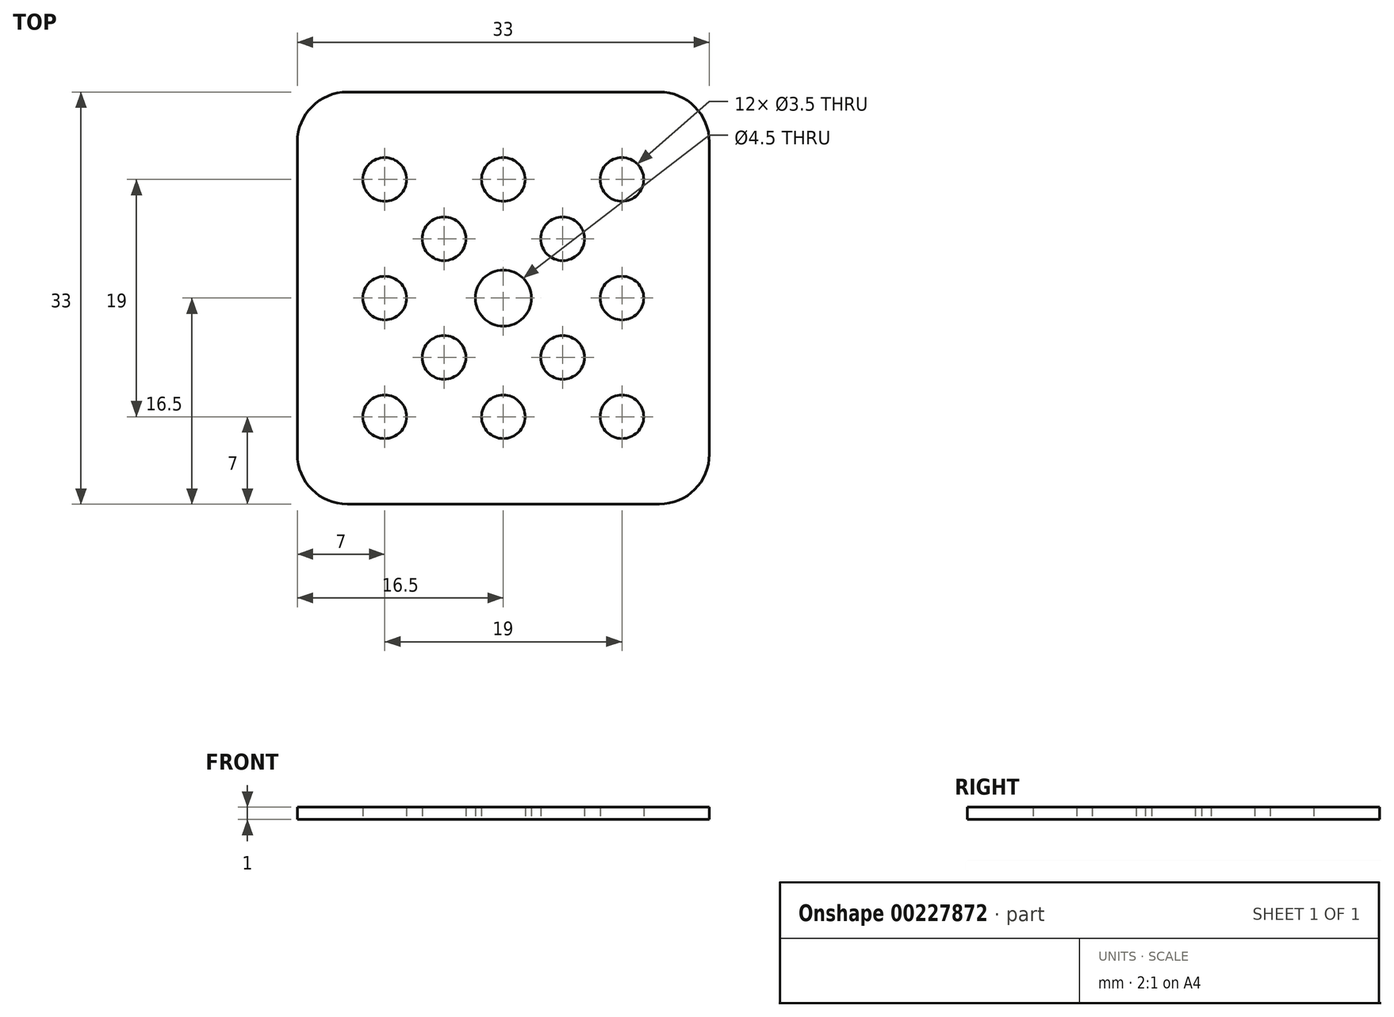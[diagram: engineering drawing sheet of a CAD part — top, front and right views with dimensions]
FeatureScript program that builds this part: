
annotation { "Feature Type Name" : "Feature", "Feature Type Description" : "" }
export const myFeature = defineFeature(function(context is Context, id is Id, definition is map)
    precondition{}
    {
        {
            var Q0;
            Q0=qCreatedBy(makeId("Top.planeOp"),FACE);
            var sketch = newSketch(context, id + "F0", { "sketchPlane" : qUnion([Q0])});
            skLineSegment(sketch, "E0.bottom", {"start": v(12.5, 16.5) * mm, "end": v(-12.5, 16.5) * mm});
            skLineSegment(sketch, "E0.top", {"start": v(12.5, -16.5) * mm, "end": v(-12.5, -16.5) * mm});
            skLineSegment(sketch, "E0.left", {"start": v(16.5, 12.5) * mm, "end": v(16.5, -12.5) * mm});
            skLineSegment(sketch, "E0.right", {"start": v(-16.5, 12.5) * mm, "end": v(-16.5, -12.5) * mm});
            skPoint(sketch, "E1.visualSharp", {"position": v(-16.5, 16.5) * mm});
            skArc(sketch, "E1.filletArc", {"start": v(-12.5, 16.5) * mm, "mid": v(-15.33, 15.33) * mm, "end": v(-16.5, 12.5) * mm});
            skPoint(sketch, "E2.visualSharp", {"position": v(16.5, 16.5) * mm});
            skArc(sketch, "E2.filletArc", {"start": v(16.5, 12.5) * mm, "mid": v(15.33, 15.33) * mm, "end": v(12.5, 16.5) * mm});
            skPoint(sketch, "E3.visualSharp", {"position": v(16.5, -16.5) * mm});
            skArc(sketch, "E3.filletArc", {"start": v(12.5, -16.5) * mm, "mid": v(15.33, -15.33) * mm, "end": v(16.5, -12.5) * mm});
            skPoint(sketch, "E4.visualSharp", {"position": v(-16.5, -16.5) * mm});
            skArc(sketch, "E4.filletArc", {"start": v(-16.5, -12.5) * mm, "mid": v(-15.33, -15.33) * mm, "end": v(-12.5, -16.5) * mm});
            skLineSegment(sketch, "E5", {"start": v(0, 0) * mm, "end": v(-9.5, -9.5) * mm, "construction": true});
            skCircle(sketch, "E6.1.1.0", {"center": v(-4.75, -4.75) * mm, "radius": 1.75 * mm});
            skLineSegment(sketch, "E6.direction1", {"start": v(-14.25, -14.25) * mm, "end": v(-4.75, -14.25) * mm, "construction": true});
            skLineSegment(sketch, "E6.direction2", {"start": v(-14.25, -14.25) * mm, "end": v(-14.25, -4.75) * mm, "construction": true});
            skCircle(sketch, "E7.0.2.1", {"center": v(4.75, -4.75) * mm, "radius": 1.75 * mm});
            skCircle(sketch, "E8.0.1.2", {"center": v(-4.75, 4.75) * mm, "radius": 1.75 * mm});
            skCircle(sketch, "E8.0.2.2", {"center": v(4.75, 4.75) * mm, "radius": 1.75 * mm});
            skCircle(sketch, "E9", {"center": v(0, 0) * mm, "radius": 2.25 * mm});
            skCircle(sketch, "E10", {"center": v(-9.5, -9.5) * mm, "radius": 1.75 * mm});
            skCircle(sketch, "E11.0.1.0", {"center": v(-9.5, 0) * mm, "radius": 1.75 * mm});
            skCircle(sketch, "E11.0.2.0", {"center": v(-9.5, 9.5) * mm, "radius": 1.75 * mm});
            skCircle(sketch, "E11.1.0.0", {"center": v(0, -9.5) * mm, "radius": 1.75 * mm});
            skCircle(sketch, "E11.1.1.0", {"center": v(0, 0) * mm, "radius": 1.75 * mm});
            skCircle(sketch, "E11.1.2.0", {"center": v(0, 9.5) * mm, "radius": 1.75 * mm});
            skCircle(sketch, "E11.2.0.0", {"center": v(9.5, -9.5) * mm, "radius": 1.75 * mm});
            skCircle(sketch, "E11.2.1.0", {"center": v(9.5, 0) * mm, "radius": 1.75 * mm});
            skCircle(sketch, "E11.2.2.0", {"center": v(9.5, 9.5) * mm, "radius": 1.75 * mm});
            skLineSegment(sketch, "E11.direction1", {"start": v(-9.5, -9.5) * mm, "end": v(0, -9.5) * mm, "construction": true});
            skLineSegment(sketch, "E11.direction2", {"start": v(-9.5, -9.5) * mm, "end": v(-9.5, 0) * mm, "construction": true});
            skSolve(sketch);
        }
        {
            var Q0;
            Q0=makeQuery(id+"F0.imprint","IMPRINT",FACE,{"disambiguationData":[TD([[makeQuery(id+"F0.imprint","IMPRINT",EDGE,{"derivedFrom":sQuery(id+"F0.wireOp",EDGE,"E0.bottom")}),1.0]])]});
            extrude(context, id + "F1", {"entities" : qUnion([Q0]), "depth" : 1 * mm});
        }
    });
